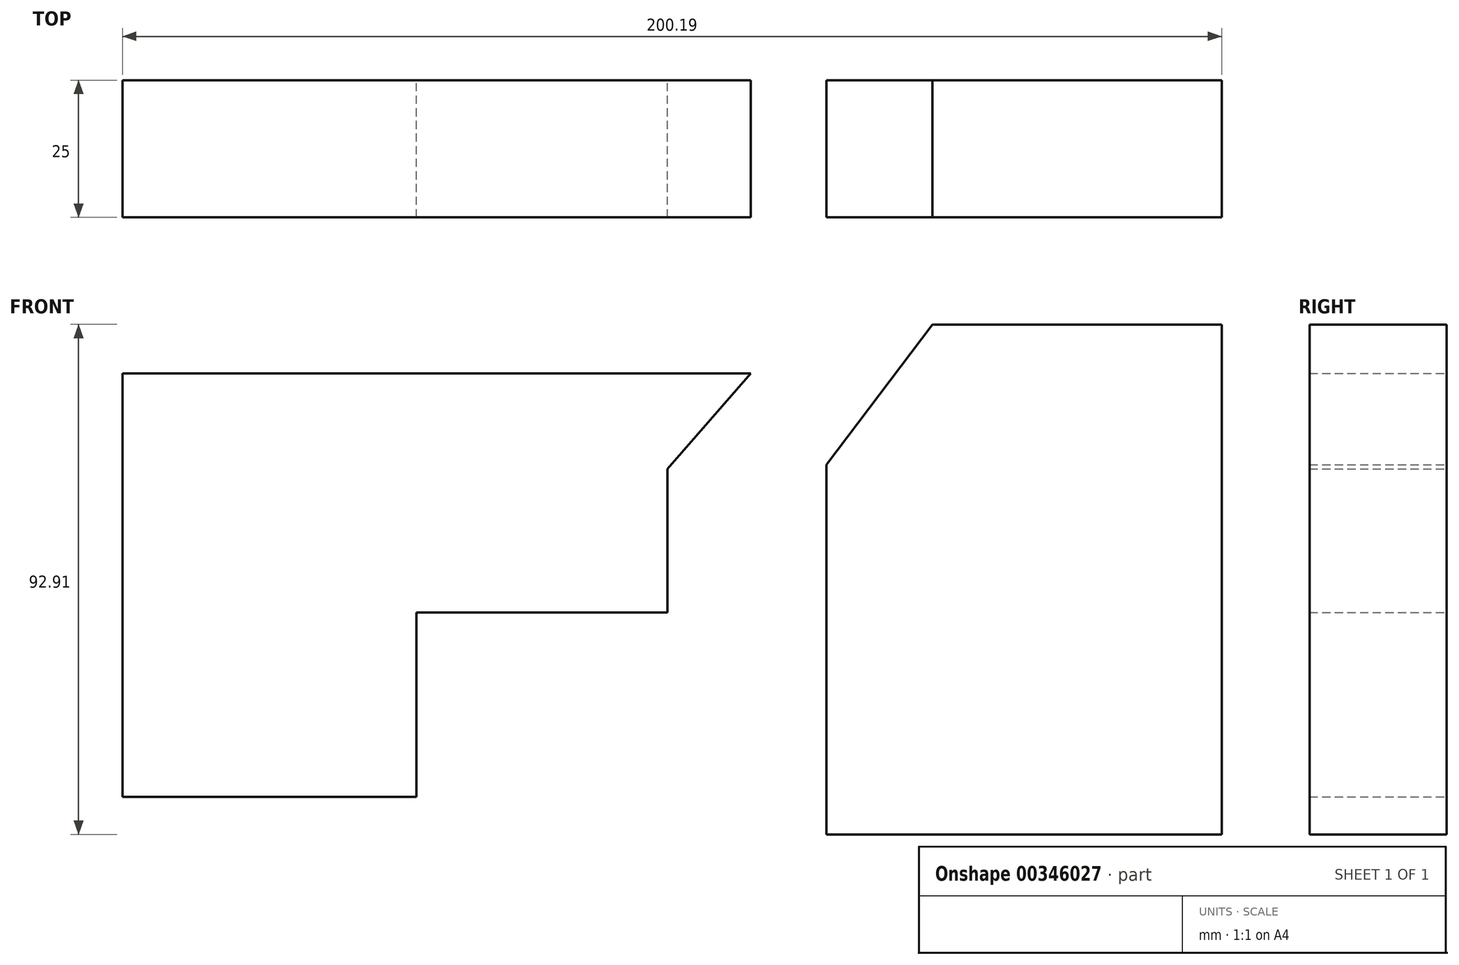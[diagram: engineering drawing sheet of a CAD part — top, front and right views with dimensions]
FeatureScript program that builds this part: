
annotation { "Feature Type Name" : "Feature", "Feature Type Description" : "" }
export const myFeature = defineFeature(function(context is Context, id is Id, definition is map)
    precondition{}
    {
        {
            var Q0;
            Q0=qCreatedBy(makeId("Front.planeOp"),FACE);
            var sketch = newSketch(context, id + "F0", { "sketchPlane" : qUnion([Q0])});
            skLineSegment(sketch, "E0", {"start": v(-122.31, 36.37) * mm, "end": v(-13.83, 36.37) * mm});
            skLineSegment(sketch, "E1", {"start": v(-13.83, 36.37) * mm, "end": v(-28.96, 19.03) * mm});
            skLineSegment(sketch, "E2", {"start": v(-28.96, 19.03) * mm, "end": v(-28.96, -7.17) * mm});
            skLineSegment(sketch, "E3", {"start": v(-28.96, -7.17) * mm, "end": v(-74.71, -7.17) * mm});
            skLineSegment(sketch, "E4", {"start": v(-74.71, -7.17) * mm, "end": v(-74.71, -40.75) * mm});
            skLineSegment(sketch, "E5", {"start": v(-74.71, -40.75) * mm, "end": v(-128.22, -40.75) * mm});
            skLineSegment(sketch, "E6", {"start": v(-128.22, -40.75) * mm, "end": v(-128.22, 36.37) * mm});
            skLineSegment(sketch, "E7", {"start": v(-128.22, 36.37) * mm, "end": v(-122.31, 36.37) * mm});
            skLineSegment(sketch, "E8", {"start": v(19.3, 45.32) * mm, "end": v(0, 19.77) * mm});
            skLineSegment(sketch, "E9", {"start": v(0, 19.77) * mm, "end": v(0, -4.96) * mm});
            skLineSegment(sketch, "E10", {"start": v(0, -4.96) * mm, "end": v(0, -35.58) * mm});
            skLineSegment(sketch, "E11", {"start": v(19.3, 45.32) * mm, "end": v(71.97, 45.32) * mm});
            skLineSegment(sketch, "E12", {"start": v(71.97, 45.32) * mm, "end": v(71.97, -47.59) * mm});
            skLineSegment(sketch, "E13", {"start": v(71.97, -47.59) * mm, "end": v(0, -47.59) * mm});
            skLineSegment(sketch, "E14", {"start": v(0, -47.59) * mm, "end": v(0, -35.58) * mm});
            skSolve(sketch);
        }
        {
            var Q0;
            Q0 = qSketchRegion(id + "F0", true);
            extrude(context, id + "F1", {"entities" : qUnion([Q0]), "depth" : 25 * mm});
        }
    });
